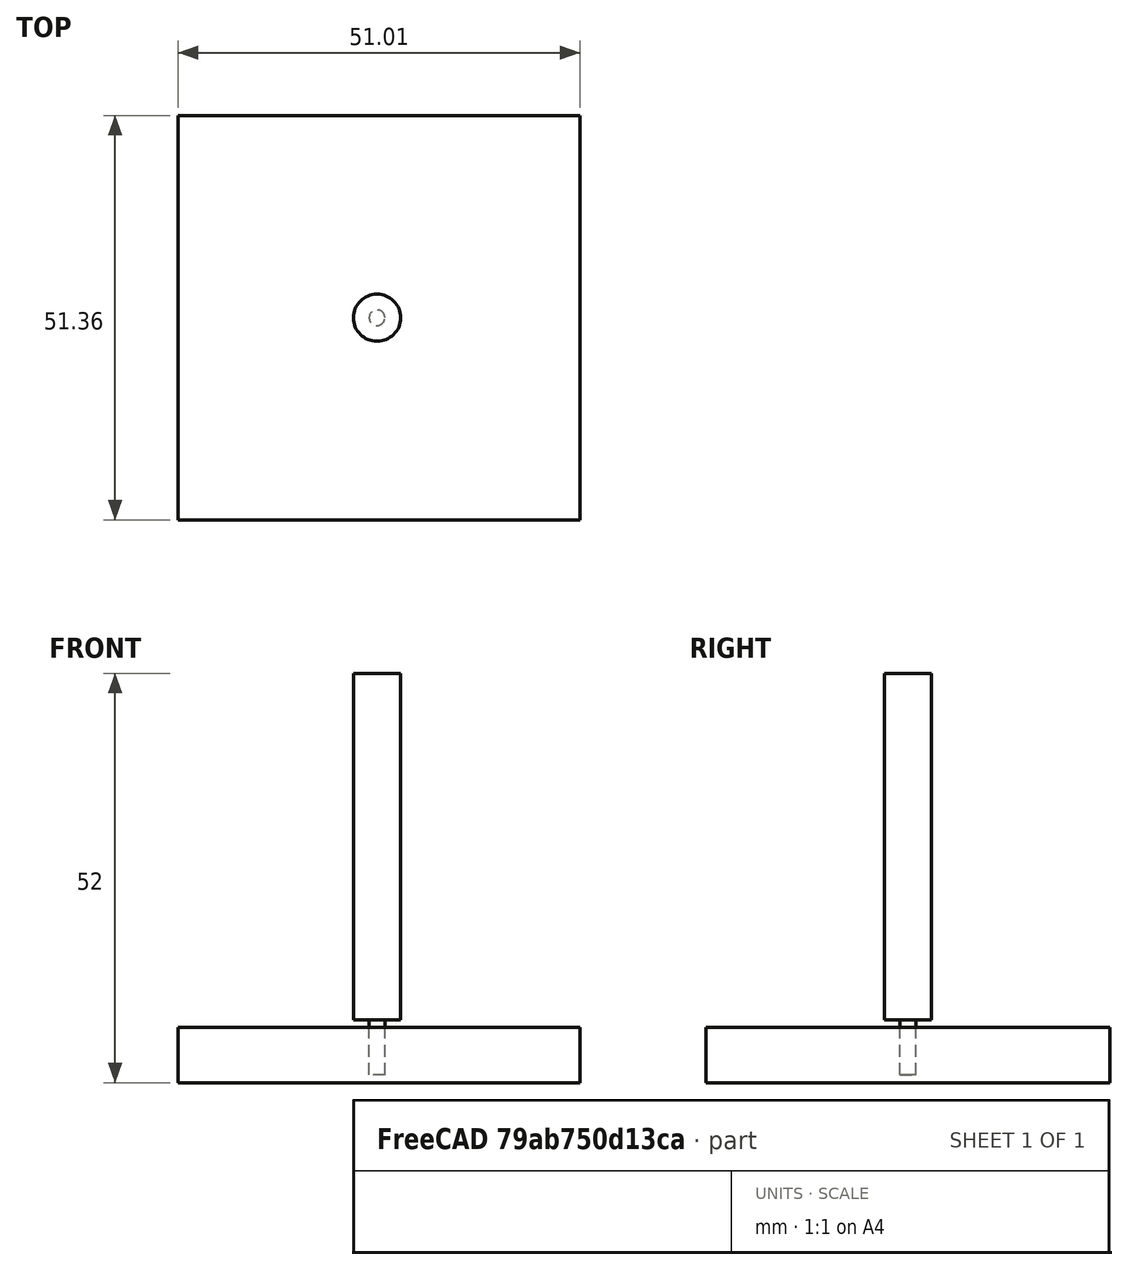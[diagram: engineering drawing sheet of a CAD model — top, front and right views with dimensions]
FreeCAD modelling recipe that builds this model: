
FCSTD DOCUMENT  (FreeCAD 0.20RUnknown)
Label: Test Involute 2
License: All rights reserved
LicenseURL: http://en.wikipedia.org/wiki/All_rights_reserved
objects: Path::FeaturePython×4, Part::FeaturePython×3, App::DocumentObjectGroup×3, Part::Part2DObjectPython×1, PartDesign::ShapeBinder×1, PartDesign::Pad×1, App::FeaturePython×1, Mesh::FeaturePython×1, Sketcher::SketchObject×1, PartDesign::Pocket×1, PartDesign::Body×1, App::MeasureDistance×1
note: 13 computed .brp shape members not serialized (recipe doc carries the construction recipe); baked Part::Feature solids carry a one-line shape summary decoded from their .brp

FEATURE [Part::Part2DObjectPython] InvoluteGear  # Draft 2D object (typed FeaturePython)
  ExternalGear = true
  HighPrecision = true
  Modules = 3.3
  NumberOfTeeth = 13
  PressureAngle = 20
FEATURE [PartDesign::ShapeBinder] ShapeBinder
  Support = -> [InvoluteGear]
  TraceSupport = false
FEATURE [PartDesign::Pad] Pad
  Direction = (0,0,1)
  Length = 5
  Length2 = 10
  Profile = -> InvoluteGear
  ReferenceAxis = -> InvoluteGear [N_Axis]
  Type = 0
FEATURE [App::FeaturePython] SetupSheet  # Path/CAM operation (typed FeaturePython)
  ClearanceHeightExpression = OpStockZMax+SetupSheet.ClearanceHeightOffset
  ClearanceHeightOffset = 5
  CoolantMode = 0
  CoolantModes = None | Flood | Mist
  FinalDepthExpression = OpFinalDepth
  HorizRapid = 0
  SafeHeightExpression = OpStockZMax+SetupSheet.SafeHeightOffset
  SafeHeightOffset = 3
  StartDepthExpression = OpStartDepth
  StepDownExpression = OpToolDiameter
  VertRapid = 0
FEATURE [Mesh::FeaturePython] CutMaterial  # WARN: FeaturePython — macro-defined, semantics opaque (R4)
FEATURE [Part::FeaturePython] ToolBit  label="2mm_Endmill"  # Path/CAM toolbit (typed FeaturePython)
  BitPropertyNames = Chipload | CuttingEdgeHeight | Diameter | Flutes | Length | Material | ShankDiameter | SpindleDirection
  BitShape = <path>
  Chipload = 0
  CuttingEdgeHeight = 7
  Diameter = 2
  File = <userpath>/Documents/Sherline/FreeCAD/Bit/2mm_Endmill.fctb
  Flutes = 2
  Length = 51
  Material = 0
  ShankDiameter = 6
  ShapeName = endmill
  SpindleDirection = 0
FEATURE [Path::FeaturePython] _mm_Endmill  label="2mm_Endmill007"  # Path/CAM operation (typed FeaturePython)
  HorizFeed = 3.33333
  HorizRapid = 0
  SpindleDir = 0
  SpindleSpeed = 4500
  Tool = -> ToolBit
  ToolNumber = 3
  VertFeed = 1
  VertRapid = 0
  expr: HorizRapid = SetupSheet.HorizRapid
  expr: VertRapid = SetupSheet.VertRapid
FEATURE [App::DocumentObjectGroup] Tools
  Group = -> [_mm_Endmill]
FEATURE [Sketcher::SketchObject] Sketch
  FullyConstrained = true
  MapMode = 5
  Placement = pos=(0,0,5) rot=(0,0,1;0rad)
  Support = -> [Pad]
  sketch-geometry (5):
    g0: ArcOfCircle CenterX=0 CenterY=0 CenterZ=0 NormalX=0 NormalY=0 NormalZ=1 AngleXU=0 Radius=7.525 StartAngle=3.48026 EndAngle=9.08612
    g1: LineSegment StartX=-11.0976 StartY=2.5 StartZ=0 EndX=-11.0976 EndY=-2.5 EndZ=0
    g2: LineSegment StartX=-11.0976 StartY=-2.5 StartZ=0 EndX=-7.09758 EndY=-2.5 EndZ=0
    g3: LineSegment StartX=-7.09758 StartY=2.5 StartZ=0 EndX=-11.0976 EndY=2.5 EndZ=0
    g4: GeomPoint X=-7.525 Y=0 Z=0
  constraints (14):
    c: Coincident(g0,g-1)
    c: Diameter(g0) = 15.05
    c: Coincident(g1,g2)
    c: Coincident(g3,g1)
    c: Horizontal(g2)
    c: Horizontal(g3)
    c: Vertical(g1)
    c: PointOnObject(g4,g0)
    c: DistanceY(g1,g1) = 5
    c: PointOnObject(g4,g-1)
    c: DistanceY(g0,g3) = 2.5
    c: Coincident(g0,g3)
    c: Coincident(g0,g2)
    c: DistanceX(g3,g3) = 4
FEATURE [PartDesign::Pocket] Pocket
  BaseFeature = -> Pad
  Direction = (0,0,-1)
  Length = 5
  Length2 = 5
  Profile = -> Sketch
  ReferenceAxis = -> Sketch [N_Axis]
  Type = 1
FEATURE [PartDesign::Body] Body
  Group = -> [InvoluteGear,ShapeBinder,Pad,Sketch,Pocket]
  Origin = -> Origin
  Tip = -> Pocket
FEATURE [Part::FeaturePython] Clone  label="Model-Body"  # Draft clone (typed FeaturePython)
  AttacherType = Attacher::AttachEngine3D
  Fuse = false
  Objects = -> [Body]
  PathResource = Model
  Scale = (1,1,1)
FEATURE [App::DocumentObjectGroup] Model
  Group = -> [Clone]
FEATURE [Part::FeaturePython] Stock  # WARN: FeaturePython — macro-defined, semantics opaque (R4)
  Base = -> Model
  ExtXneg = 1
  ExtXpos = 1
  ExtYneg = 1
  ExtYpos = 1
  ExtZneg = 1
  ExtZpos = 1
  Placement = pos=(-24.2635,-24.6778,0) rot=(0,0,1;0rad)
  StockType = FromBase
FEATURE [Path::FeaturePython] Profile  label="Gear"  # Path/CAM operation (typed FeaturePython)
  Active = true
  AreaParams:
    Tolerance = 1e-07
    FitArcs = True
    Simplify = False
    CleanDistance = 0.0
    Accuracy = 0.01
    Unit = 1.0
    MinArcPoints = 4
    MaxArcPoints = 100
    ClipperScale = 10000000.0
    Fill = 0
    Coplanar = 0
    Reorient = True
    Outline = False
    Explode = False
    OpenMode = 0
    Deflection = 0.01
    SubjectFill = 0
    ClipFill = 0
    Offset = 1.0
    ExtraPass = 0
    Stepover = 0.0
    LastStepover = 0.0
    JoinType = 0
    EndType = 0
    MiterLimit = 2.0
    RoundPrecision = 0.0
    PocketMode = 0
    ToolRadius = 1.0
    PocketExtraOffset = 0.0
    PocketStepover = 0.0
    PocketLastStepover = 0.0
    FromCenter = False
    Angle = 45.0
    AngleShift = 0.0
    Shift = 0.0
    Thicken = False
    SectionCount = -1
    Stepdown = 1.0
    SectionOffset = 0.0
    SectionTolerance = 1e-06
    SectionMode = 2
    Project = False
  Base = -> [Clone]
  ClearanceHeight = 11
  CoolantMode = 0
  CycleTime = 00:06:08
  Direction = 0
  FinalDepth = 0
  HandleMultipleFeatures = 0
  JoinType = 0
  MiterLimit = 0.1
  OffsetExtra = 0
  OpFinalDepth = 5
  OpStartDepth = 6
  OpStockZMax = 6
  OpStockZMin = -1
  OpToolDiameter = 2
  PathParams = {'orientation': 1, 'feedrate': 3.3333333333333335, 'feedrate_v': 1.0, 'verbose': True, 'resume_height': 9.0, 'retraction': 11.0, 'return_end': True, 'preamble': False}
  SafeHeight = 9
  Side = 0
  SplitArcs = false
  StartDepth = 5
  StartPoint = (0,0,0)
  StepDown = 1
  ToolController = -> _mm_Endmill
  UseComp = true
  UseStartPoint = false
  processCircles = false
  processHoles = false
  processPerimeter = true
  expr: ClearanceHeight = OpStockZMax + SetupSheet.ClearanceHeightOffset
  expr: FinalDepth = 0
  expr: SafeHeight = OpStockZMax + SetupSheet.SafeHeightOffset
  expr: StartDepth = 5
  expr: StepDown = 1
FEATURE [App::MeasureDistance] Distance  label="Distance: 49.18 mm"
  Distance = 49.1809
  P1 = (-23.9767,-5.84382,5)
  P2 = (22.3847,10.5689,5)
FEATURE [Path::FeaturePython] Profile001  label="Hole"  # Path/CAM operation (typed FeaturePython)
  Active = true
  AreaParams:
    Tolerance = 1e-07
    FitArcs = True
    Simplify = False
    CleanDistance = 0.0
    Accuracy = 0.01
    Unit = 1.0
    MinArcPoints = 4
    MaxArcPoints = 100
    ClipperScale = 10000000.0
    Fill = 0
    Coplanar = 0
    Reorient = True
    Outline = False
    Explode = False
    OpenMode = 0
    Deflection = 0.01
    SubjectFill = 0
    ClipFill = 0
    Offset = -1.0
    ExtraPass = 0
    Stepover = 0.0
    LastStepover = 0.0
    JoinType = 0
    EndType = 0
    MiterLimit = 2.0
    RoundPrecision = 0.0
    PocketMode = 0
    ToolRadius = 1.0
    PocketExtraOffset = 0.0
    PocketStepover = 0.0
    PocketLastStepover = 0.0
    FromCenter = False
    Angle = 45.0
    AngleShift = 0.0
    Shift = 0.0
    Thicken = False
    SectionCount = -1
    Stepdown = 1.0
    SectionOffset = 0.0
    SectionTolerance = 1e-06
    SectionMode = 2
    Project = False
  Base = -> [Clone]
  ClearanceHeight = 11
  CoolantMode = 0
  CycleTime = 00:01:45
  Direction = 0
  FinalDepth = 0
  HandleMultipleFeatures = 0
  JoinType = 0
  MiterLimit = 0.1
  OffsetExtra = 0
  OpFinalDepth = 5
  OpStartDepth = 6
  OpStockZMax = 6
  OpStockZMin = -1
  OpToolDiameter = 2
  PathParams = {'orientation': 1, 'feedrate': 3.3333333333333335, 'feedrate_v': 1.0, 'verbose': True, 'resume_height': 9.0, 'retraction': 11.0, 'return_end': True, 'preamble': False}
  SafeHeight = 9
  Side = 1
  SplitArcs = false
  StartDepth = 5
  StartPoint = (0,0,0)
  StepDown = 1
  ToolController = -> _mm_Endmill
  UseComp = true
  UseStartPoint = false
  processCircles = false
  processHoles = false
  processPerimeter = true
  expr: ClearanceHeight = OpStockZMax + SetupSheet.ClearanceHeightOffset
  expr: FinalDepth = 0
  expr: SafeHeight = OpStockZMax + SetupSheet.SafeHeightOffset
  expr: StartDepth = 5
  expr: StepDown = 1
FEATURE [App::DocumentObjectGroup] Operations
  Group = -> [Profile001,Profile]
FEATURE [Path::FeaturePython] Job  # Path/CAM operation (typed FeaturePython)
  CycleTime = 00:07:53
  Fixtures = G54
  GeometryTolerance = 0.01
  JobType = 0
  LastPostProcessDate = 2023-04-17 16:18:32.581872
  LastPostProcessOutput = <userpath>/MensShed/CNCRouter/WaveTank/Test Involute 2-Job.ngc
  Model = -> Model
  Operations = -> Operations
  OrderOutputBy = 0
  PostProcessor = 2
  PostProcessorOutputFile = %D/%d-%j.ngc
  SetupSheet = -> SetupSheet
  SplitOutput = false
  Stock = -> Stock
  Tools = -> Tools
note: 1 file-system path scrubbed to <path> (originals preserved in the JSON sidecar)
